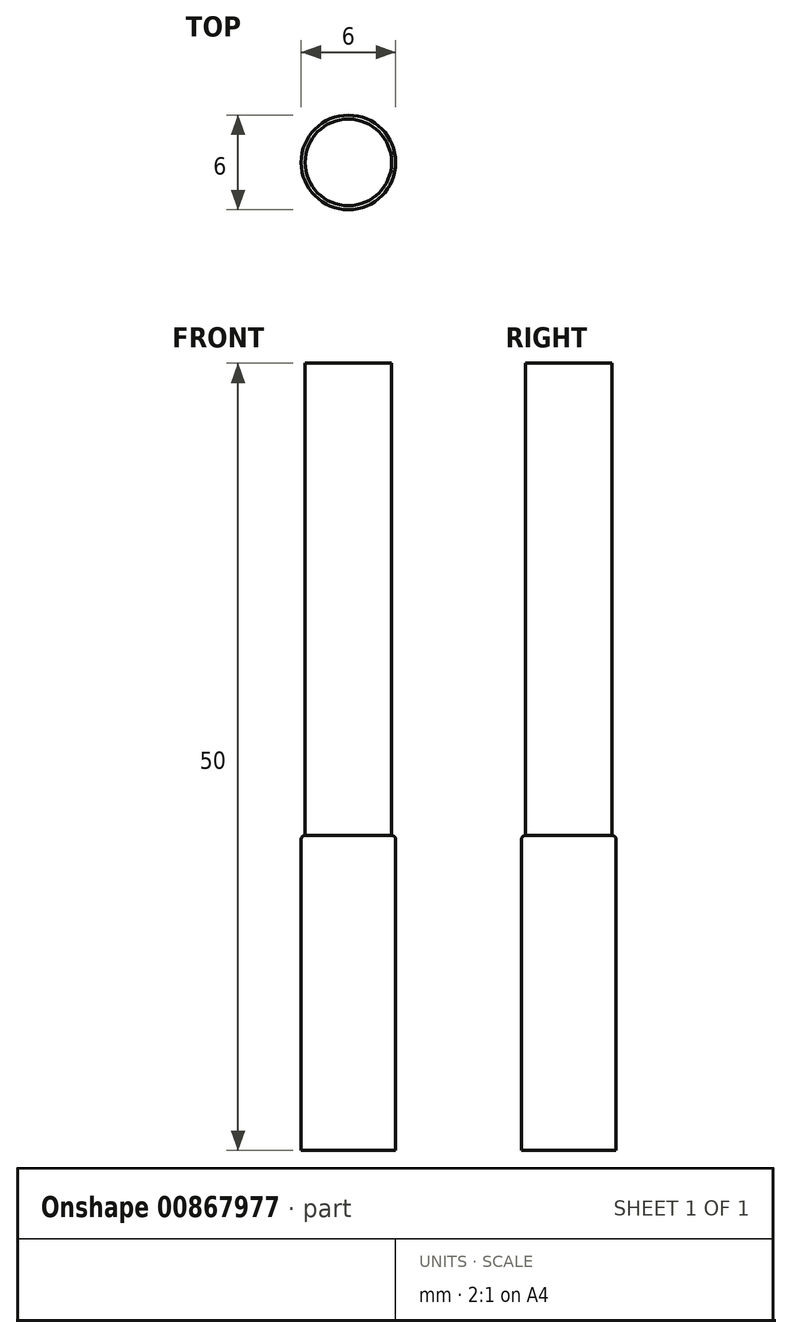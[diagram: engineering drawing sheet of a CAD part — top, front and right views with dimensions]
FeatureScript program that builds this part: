
annotation { "Feature Type Name" : "Feature", "Feature Type Description" : "" }
export const myFeature = defineFeature(function(context is Context, id is Id, definition is map)
    precondition{}
    {
        {
            var Q0;
            Q0=qCreatedBy(makeId("Front.planeOp"),FACE);
            var sketch = newSketch(context, id + "F0", { "sketchPlane" : qUnion([Q0])});
            skLineSegment(sketch, "E0", {"start": v(0, 0) * mm, "end": v(2.75, 0) * mm});
            skLineSegment(sketch, "E1", {"start": v(2.75, 0) * mm, "end": v(2.75, -30) * mm});
            skArc(sketch, "E2", {"start": v(3, -30.25) * mm, "mid": v(2.93, -30.07) * mm, "end": v(2.75, -30) * mm});
            skLineSegment(sketch, "E3", {"start": v(3, -30.25) * mm, "end": v(3, -50) * mm});
            skLineSegment(sketch, "E4", {"start": v(3, -50) * mm, "end": v(0, -50) * mm});
            skLineSegment(sketch, "E5", {"start": v(0, -50) * mm, "end": v(0, 0) * mm});
            skSolve(sketch);
        }
        {
            var Q0;
            Q0=makeQuery(id+"F0.imprint","IMPRINT",FACE,{"disambiguationData":[TD([[makeQuery(id+"F0.imprint","IMPRINT",EDGE,{"derivedFrom":sQuery(id+"F0.wireOp",EDGE,"E0")}),-1.0]])]});
            var Q1;
            Q1=sQuery(id+"F0.wireOp",EDGE,"E5");
            revolve(context, id + "F1", {"surfaceOperationType" : NewSurfaceOperationType.NEW, "entities" : qUnion([Q0]), "axis" : qUnion([Q1]), "revolveType" : RevolveType.FULL});
        }
    });
